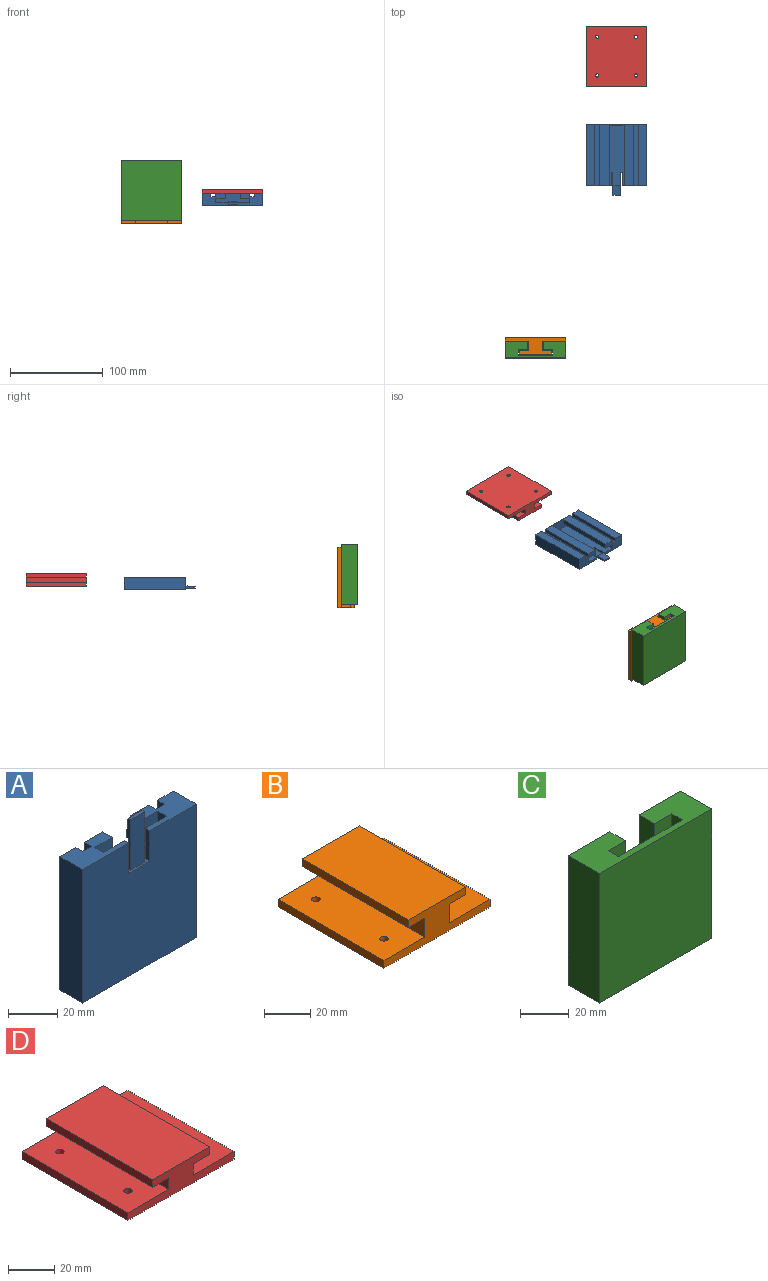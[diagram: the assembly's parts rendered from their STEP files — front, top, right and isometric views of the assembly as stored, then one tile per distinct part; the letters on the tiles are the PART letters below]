
ASSEMBLY  parts=4 mates=4
PART A: 32 faces, bbox 65x13x76 mm
  f0: plane 66x9.14mm, normal (0,1,0), area 603.3mm2, adj f5,f11,f16,f31
  f1: plane 66x36.72mm, normal (0,1,0), area 1383.5mm2, adj f4,f5,f9,f14,f15,f16,f28,f29
  f2: plane 65x36mm, normal (0,1,0), area 2280mm2, adj f4,f5,f7,f12,f15,f17,f18,f19
  f3: plane 66x65mm, normal (0,-1,0), area 4110mm2, adj f4,f5,f6,f11,f16,f17,f18,f22
  f4: plane 26.5x13mm, normal (0,0,1), area 253.5mm2, adj f1,f2,f3,f6,f7,f8,f9,f10
  f5: plane 26.5x13mm, normal (0,0,1), area 253.5mm2, adj f0,f1,f2,f3,f11,f12,f13,f14
  f6: plane 66x13mm, normal (-1,0,0), area 858mm2, adj f3,f4,f10,f16
  f7: plane 65x5mm, normal (1,0,0), area 325mm2, adj f2,f4,f8,f15
  f8: plane 65x10mm, normal (0,-1,0), area 650mm2, adj f4,f7,f9,f15
  f9: plane 65x5.5mm, normal (1,0,0), area 357.5mm2, adj f1,f4,f8,f15
  f10: plane 66x9.14mm, normal (0,1,0), area 603.3mm2, adj f4,f6,f16,f26
  f11: plane 66x13mm, normal (1,0,0), area 858mm2, adj f0,f3,f5,f16
  f12: plane 65x5mm, normal (-1,0,0), area 325mm2, adj f2,f5,f13,f15
  f13: plane 65x10mm, normal (0,-1,0), area 650mm2, adj f5,f12,f14,f15
  f14: plane 65x5.5mm, normal (-1,0,0), area 357.5mm2, adj f1,f5,f13,f15
  f15: plane 36x10.5mm, normal (0,0,1), area 268mm2, adj f1,f2,f7,f8,f9,f12,f13,f14
  f16: plane 65x13mm, normal (0,0,-1), area 805mm2, adj f0,f1,f3,f6,f10,f11,f26,f27
  f17: plane 15x2.5mm, normal (1,0,0), area 37.5mm2, adj f2,f3,f4,f22
  f18: plane 15x2.5mm, normal (-1,0,0), area 37.5mm2, adj f2,f3,f5,f22
  f19: plane 25x2.5mm, normal (1,0,0), area 42.5mm2, adj f2,f20,f22,f23,f24,f25
  f20: plane 25x8mm, normal (0,-1,0), area 200mm2, adj f19,f21,f22,f23
  f21: plane 25x2.5mm, normal (-1,0,0), area 42.5mm2, adj f2,f20,f22,f23,f24,f25
  f22: plane 12x2.5mm, normal (0,0,1), area 18mm2, adj f2,f3,f17,f18,f19,f20,f21
  f23: plane 8x1.5mm, normal (0,0,1), area 12mm2, adj f19,f20,f21,f24
  f24: plane 10x8mm, normal (0,1,0.1), area 80.4mm2, adj f19,f21,f23,f25
  f25: plane 8x1mm, normal (0,0,-1), area 8mm2, adj f2,f19,f21,f24
  f26: plane 66x4mm, normal (1,0,0), area 264mm2, adj f4,f10,f16,f27
  f27: plane 66x5mm, normal (0,1,0), area 330mm2, adj f4,f16,f26,f28
  f28: plane 66x4mm, normal (-1,0,0), area 264mm2, adj f1,f4,f16,f27
  f29: plane 66x4mm, normal (1,0,0), area 264mm2, adj f1,f5,f16,f30
  f30: plane 66x5mm, normal (0,1,0), area 330mm2, adj f5,f16,f29,f31
  f31: plane 66x4mm, normal (-1,0,0), area 264mm2, adj f0,f5,f16,f30
PART B: 18 faces, bbox 65x65x18 mm
  f0: plane 65x35mm, normal (0,0,1), area 2275mm2, adj f1,f7,f8,f9
  f1: plane 65x4mm, normal (-1,0,0), area 260mm2, adj f0,f2,f7,f8
  f2: plane 65x10mm, normal (0,0,-1), area 650mm2, adj f1,f3,f7,f8
  f3: plane 65x10mm, normal (-1,0,0), area 650mm2, adj f2,f4,f7,f8
  f4: plane 65x25mm, normal (0,0,1), area 1604.6mm2, adj f3,f5,f7,f8,f16,f17
  f5: plane 65x4mm, normal (-1,0,0), area 260mm2, adj f4,f6,f7,f8
  f6: plane 65x65mm, normal (0,0,-1), area 4184.3mm2, adj f5,f7,f8,f13,f14,f15,f16,f17
  f7: plane 65x18mm, normal (0,-1,0), area 550mm2, adj f0,f1,f2,f3,f4,f5,f6,f9
  f8: plane 65x18mm, normal (0,1,0), area 550mm2, adj f0,f1,f2,f3,f4,f5,f6,f9
  f9: plane 65x4mm, normal (1,0,0), area 260mm2, adj f0,f7,f8,f10
  f10: plane 65x10mm, normal (0,0,-1), area 650mm2, adj f7,f8,f9,f11
  f11: plane 65x10mm, normal (1,0,0), area 650mm2, adj f7,f8,f10,f12
  f12: plane 65x25mm, normal (0,0,1), area 1604.6mm2, adj f7,f8,f11,f13,f14,f15
  f13: plane 65x4mm, normal (1,0,0), area 260mm2, adj f6,f7,f8,f12
  f14: cylinder r=1.8mm len=4mm, axis (0,0,-1), area 45.2mm2, adj f6,f12
  f15: cylinder r=1.8mm len=4mm, axis (0,0,-1), area 45.2mm2, adj f6,f12
  f16: cylinder r=1.8mm len=4mm, axis (0,0,-1), area 45.2mm2, adj f4,f6
  f17: cylinder r=1.8mm len=4mm, axis (0,0,-1), area 45.2mm2, adj f4,f6
PART C: 14 faces, bbox 65x18x65 mm
  f0: plane 65x18mm, normal (-1,0,0), area 1170mm2, adj f1,f6,f7,f8
  f1: plane 65x65mm, normal (0,-1,0), area 4225mm2, adj f0,f7,f8,f9
  f2: plane 65x37mm, normal (0,1,0), area 2405mm2, adj f3,f7,f8,f10
  f3: plane 65x6mm, normal (1,0,0), area 390mm2, adj f2,f4,f7,f8
  f4: plane 65x10mm, normal (0,-1,0), area 650mm2, adj f3,f5,f7,f8
  f5: plane 65x9mm, normal (1,0,0), area 585mm2, adj f4,f6,f7,f8
  f6: plane 65x24mm, normal (0,1,0), area 1560mm2, adj f0,f5,f7,f8
  f7: plane 65x18mm, normal (0,0,1), area 795mm2, adj f0,f1,f2,f3,f4,f5,f6,f9
  f8: plane 65x18mm, normal (0,0,-1), area 795mm2, adj f0,f1,f2,f3,f4,f5,f6,f9
  f9: plane 65x18mm, normal (1,0,0), area 1170mm2, adj f1,f7,f8,f13
  f10: plane 65x6mm, normal (-1,0,0), area 390mm2, adj f2,f7,f8,f11
  f11: plane 65x10mm, normal (0,-1,0), area 650mm2, adj f7,f8,f10,f12
  f12: plane 65x9mm, normal (-1,0,0), area 585mm2, adj f7,f8,f11,f13
  f13: plane 65x24mm, normal (0,1,0), area 1560mm2, adj f7,f8,f9,f12
PART D: 18 faces, bbox 65x65x14 mm
  f0: plane 65x35mm, normal (0,0,1), area 2275mm2, adj f1,f7,f8,f9
  f1: plane 65x4mm, normal (-1,0,0), area 260mm2, adj f0,f2,f7,f8
  f2: plane 65x10mm, normal (0,0,-1), area 650mm2, adj f1,f3,f7,f8
  f3: plane 65x6mm, normal (-1,0,0), area 390mm2, adj f2,f4,f7,f8
  f4: plane 65x25mm, normal (0,0,1), area 1604.6mm2, adj f3,f5,f7,f8,f16,f17
  f5: plane 65x4mm, normal (-1,0,0), area 260mm2, adj f4,f6,f7,f8
  f6: plane 65x65mm, normal (0,0,-1), area 4184.3mm2, adj f5,f7,f8,f13,f14,f15,f16,f17
  f7: plane 65x14mm, normal (0,-1,0), area 490mm2, adj f0,f1,f2,f3,f4,f5,f6,f9
  f8: plane 65x14mm, normal (0,1,0), area 490mm2, adj f0,f1,f2,f3,f4,f5,f6,f9
  f9: plane 65x4mm, normal (1,0,0), area 260mm2, adj f0,f7,f8,f10
  f10: plane 65x10mm, normal (0,0,-1), area 650mm2, adj f7,f8,f9,f11
  f11: plane 65x6mm, normal (1,0,0), area 390mm2, adj f7,f8,f10,f12
  f12: plane 65x25mm, normal (0,0,1), area 1604.6mm2, adj f7,f8,f11,f13,f14,f15
  f13: plane 65x4mm, normal (1,0,0), area 260mm2, adj f6,f7,f8,f12
  f14: cylinder r=1.8mm len=4mm, axis (0,0,-1), area 45.2mm2, adj f6,f12
  f15: cylinder r=1.8mm len=4mm, axis (0,0,-1), area 45.2mm2, adj f6,f12
  f16: cylinder r=1.8mm len=4mm, axis (0,0,-1), area 45.2mm2, adj f4,f6
  f17: cylinder r=1.8mm len=4mm, axis (0,0,-1), area 45.2mm2, adj f4,f6
PLACE A rot(axis=(1,0,0),90deg) t=(75.08,244.19,-53.24)mm fixed
PLACE B rot(axis=(1,0,0),90deg) t=(19.98,6.63,-40.73)mm fixed
PLACE C t=(-12.52,-6.37,-70.05)mm
PLACE D rot(axis=(1,0,0),180deg) t=(107.58,319.28,-43.74)mm
MATE planar B.f12 <-> C.f13  axis (0,-1,0) through (27.48,11.63,-8.23)mm
MATE planar D.f12 <-> A.f1  axis (0,0,-1) through (127.57,319.28,-40.24)mm
MATE planar D.f13 <-> A.f11  axis (1,0,0) through (140.08,319.28,-38.24)mm
MATE planar B.f13 <-> C.f9  axis (1,0,0) through (52.48,13.63,-40.73)mm
